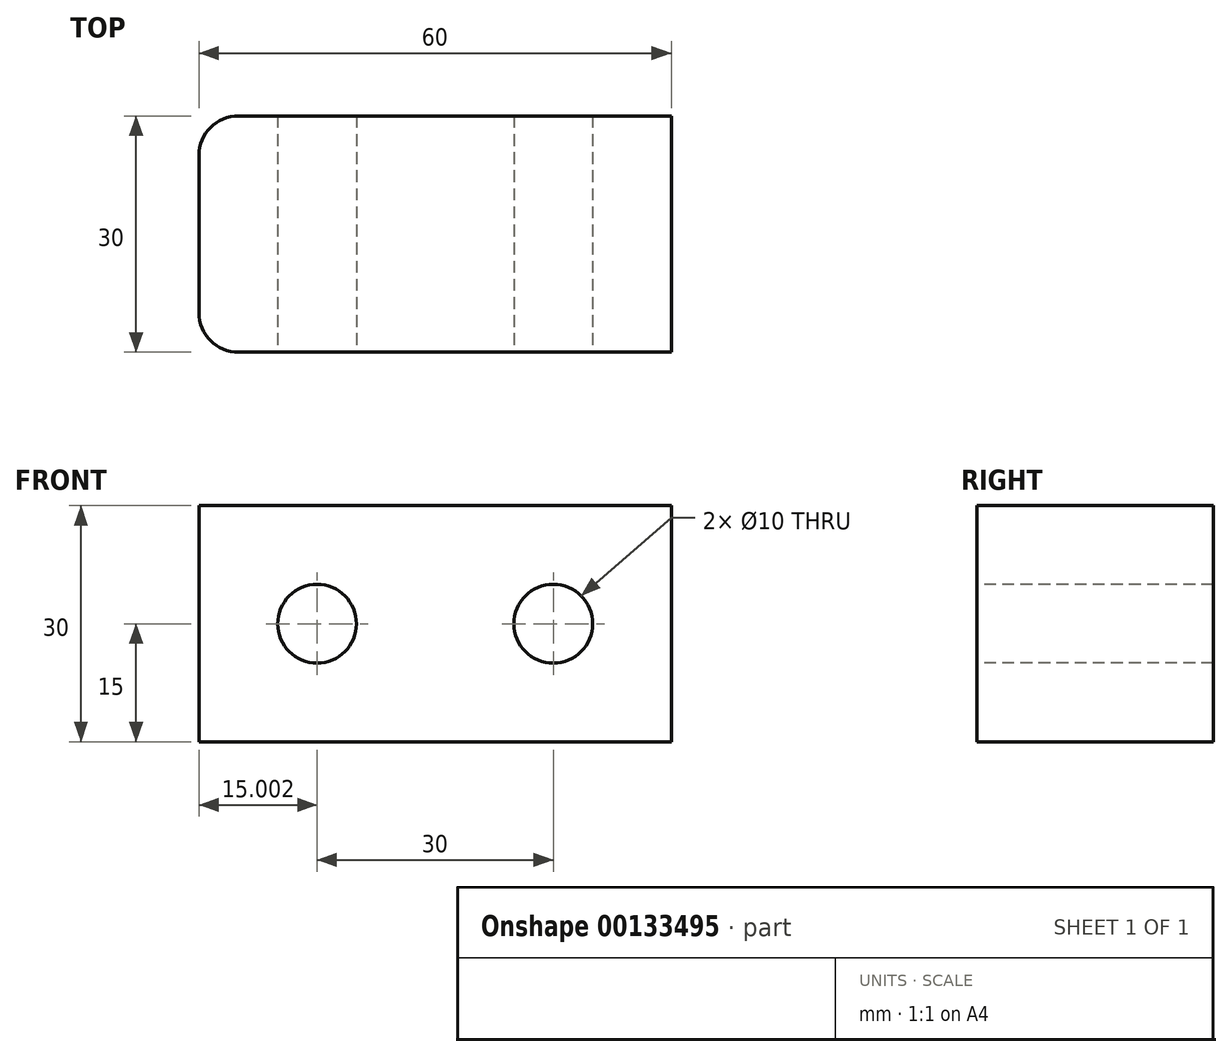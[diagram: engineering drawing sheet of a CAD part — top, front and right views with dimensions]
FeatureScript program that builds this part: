
annotation { "Feature Type Name" : "Feature", "Feature Type Description" : "" }
export const myFeature = defineFeature(function(context is Context, id is Id, definition is map)
    precondition{}
    {
        {
            var Q0;
            Q0=qCreatedBy(makeId("Top.planeOp"),FACE);
            var sketch = newSketch(context, id + "F0", { "sketchPlane" : qUnion([Q0])});
            skLineSegment(sketch, "E0.bottom", {"start": v(-185.86, -179.96) * mm, "end": v(-155.86, -179.96) * mm});
            skLineSegment(sketch, "E0.top", {"start": v(-185.86, -209.96) * mm, "end": v(-155.86, -209.96) * mm});
            skLineSegment(sketch, "E0.left", {"start": v(-185.86, -179.96) * mm, "end": v(-185.86, -209.96) * mm});
            skLineSegment(sketch, "E0.right", {"start": v(-155.86, -179.96) * mm, "end": v(-155.86, -209.96) * mm});
            skSolve(sketch);
        }
        {
            var Q0;
            Q0=makeQuery(id+"F0.imprint","IMPRINT",FACE,{"disambiguationData":[TD([[makeQuery(id+"F0.imprint","IMPRINT",EDGE,{"derivedFrom":sQuery(id+"F0.wireOp",EDGE,"E0.bottom")}),-1.0]])]});
            extrude(context, id + "F1", {"entities" : qUnion([Q0]), "depth" : 30 * mm});
        }
        {
            var Q0;
            Q0=makeQuery(id+"F1.opExtrude","SWEPT_FACE",FACE,{"disambiguationData":[OSD([sQuery(id+"F0.wireOp",EDGE,"E0.top")])]});
            var sketch = newSketch(context, id + "F2", { "sketchPlane" : qUnion([Q0])});
            skLineSegment(sketch, "E1", {"start": v(-170.86, 30) * mm, "end": v(-170.86, 15) * mm});
            skCircle(sketch, "E2", {"center": v(-170.86, 15) * mm, "radius": 5 * mm});
            skSolve(sketch);
        }
        {
            var Q0;
            Q0 = qSketchRegion(id + "F2", true);
            extrude(context, id + "F3", {"entities" : qUnion([Q0]), "operationType" : NewBodyOperationType.REMOVE, "endBound" : BoundingType.THROUGH_ALL, "oppositeDirection" : true, "depth" : 25 * mm});
        }
        {
            var Q0;
            Q0=makeQuery(id+"F1.opExtrude","SWEPT_BODY",BODY,{"disambiguationData":[OSD([sQuery(id+"F0.wireOp",EDGE,"E0.bottom"),sQuery(id+"F0.wireOp",EDGE,"E0.top"),sQuery(id+"F0.wireOp",EDGE,"E0.left"),sQuery(id+"F0.wireOp",EDGE,"E0.right")])]});
            var Q1;
            Q1=makeQuery(id+"F1.opExtrude","SWEPT_FACE",FACE,{"disambiguationData":[OSD([sQuery(id+"F0.wireOp",EDGE,"E0.left")])]});
            mirror(context, id + "F4", {"operationType" : NewBodyOperationType.ADD, "entities" : qUnion([Q0]), "mirrorPlane" : qUnion([Q1])});
        }
        {
            var Q0;
            Q0=makeQuery(id+"F4.opPattern","COPY",EDGE,{"derivedFrom":makeQuery(id+"F1.opExtrude","SWEPT_EDGE",EDGE,{"disambiguationData":[OSD([sQuery(id+"F0.wireOp",EDGE,"E0.top"),sQuery(id+"F0.wireOp",EDGE,"E0.right")])]}),"instanceName":"1"});
            fillet(context, id + "F5", {"entities" : qUnion([Q0]), "radius" : 5 * mm, "tangentPropagation" : true, "allowEdgeOverflow" : false});
        }
        {
            var Q0;
            Q0=makeQuery(id+"F4.opPattern","COPY",EDGE,{"derivedFrom":makeQuery(id+"F1.opExtrude","SWEPT_EDGE",EDGE,{"disambiguationData":[OSD([sQuery(id+"F0.wireOp",EDGE,"E0.bottom"),sQuery(id+"F0.wireOp",EDGE,"E0.right")])]}),"instanceName":"1"});
            var Q1;
            Q1=makeQuery(id+"F4.opPattern","COPY",EDGE,{"derivedFrom":makeQuery(id+"F3.boolean.opBoolean","COPY",EDGE,{"derivedFrom":makeQuery(id+"F3.opExtrude","CAP_EDGE",EDGE,{"disambiguationData":[OSD([sQuery(id+"F2.wireOp",EDGE,"E2")])],"isStart":true})}),"instanceName":"1"});
            fillet(context, id + "F6", {"entities" : qUnion([Q0, Q1]), "radius" : 5 * mm, "tangentPropagation" : true, "allowEdgeOverflow" : false});
        }
    });
